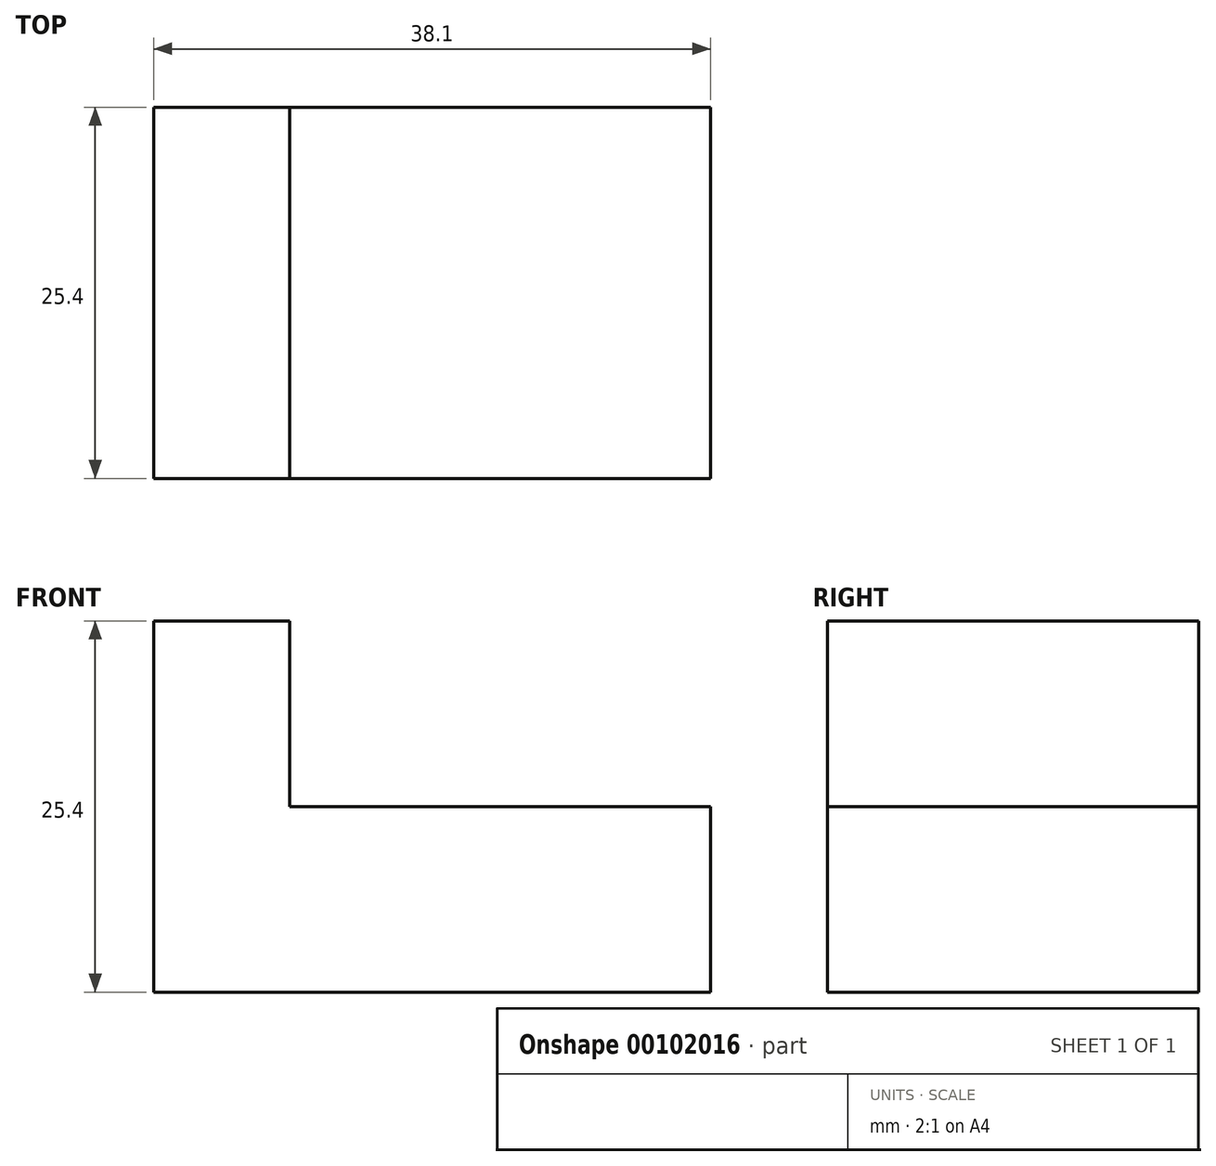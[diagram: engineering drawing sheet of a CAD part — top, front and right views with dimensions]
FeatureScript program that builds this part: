
annotation { "Feature Type Name" : "Feature", "Feature Type Description" : "" }
export const myFeature = defineFeature(function(context is Context, id is Id, definition is map)
    precondition{}
    {
        {
            var Q0;
            Q0=qCreatedBy(makeId("Top.planeOp"),FACE);
            var sketch = newSketch(context, id + "F0", { "sketchPlane" : qUnion([Q0])});
            skLineSegment(sketch, "E0", {"start": v(0, 0) * mm, "end": v(38.1, 0) * mm});
            skLineSegment(sketch, "E1", {"start": v(38.1, 0) * mm, "end": v(38.1, 25.4) * mm});
            skLineSegment(sketch, "E2", {"start": v(38.1, 25.4) * mm, "end": v(0, 25.4) * mm});
            skLineSegment(sketch, "E3", {"start": v(0, 25.4) * mm, "end": v(0, 0) * mm});
            skSolve(sketch);
        }
        {
            var Q0;
            Q0=makeQuery(id+"F0.imprint","IMPRINT",FACE,{"disambiguationData":[TD([[makeQuery(id+"F0.imprint","IMPRINT",EDGE,{"derivedFrom":sQuery(id+"F0.wireOp",EDGE,"E0")}),1.0]])]});
            extrude(context, id + "F1", {"entities" : qUnion([Q0]), "depth" : 12.7 * mm});
        }
        {
            var Q0;
            Q0=makeQuery(id+"F1.opExtrude","CAP_FACE",FACE,{"disambiguationData":[OSD([sQuery(id+"F0.wireOp",EDGE,"E0"),sQuery(id+"F0.wireOp",EDGE,"E1"),sQuery(id+"F0.wireOp",EDGE,"E2"),sQuery(id+"F0.wireOp",EDGE,"E3")])],"isStart":false});
            var sketch = newSketch(context, id + "F2", { "sketchPlane" : qUnion([Q0])});
            skLineSegment(sketch, "E4", {"start": v(0, 25.4) * mm, "end": v(9.29, 25.4) * mm});
            skLineSegment(sketch, "E5", {"start": v(9.29, 25.4) * mm, "end": v(9.29, 0) * mm});
            skLineSegment(sketch, "E6", {"start": v(9.29, 0) * mm, "end": v(0, 0) * mm});
            skLineSegment(sketch, "E7", {"start": v(0, 0) * mm, "end": v(0, 25.4) * mm});
            skSolve(sketch);
        }
        {
            var Q0;
            Q0=makeQuery(id+"F2.imprint","IMPRINT",FACE,{"disambiguationData":[TD([[makeQuery(id+"F2.imprint","IMPRINT",EDGE,{"derivedFrom":sQuery(id+"F2.wireOp",EDGE,"E4")}),1.0]])]});
            extrude(context, id + "F3", {"entities" : qUnion([Q0]), "operationType" : NewBodyOperationType.ADD, "depth" : 12.7 * mm});
        }
    });
